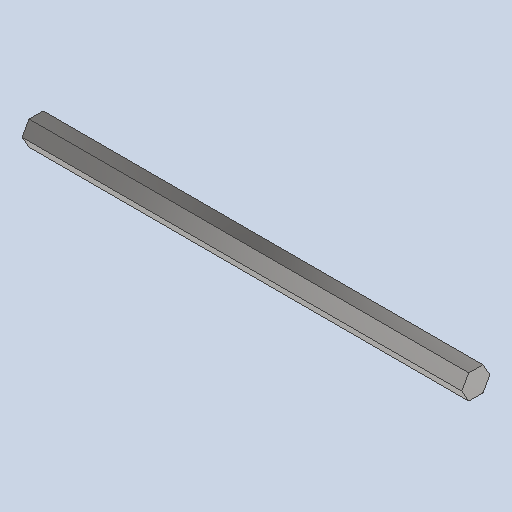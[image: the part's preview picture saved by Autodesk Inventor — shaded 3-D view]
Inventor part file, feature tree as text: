
AUTODESK INVENTOR PART (.ipt)
format: ipt  version: 2023 (Build 270158000, 158)  size: 96,256 bytes
history: native  units: in
note: dims shown in document units (in); Inventor stores cm internally (conversion verified against a paired STEP export)
features: extrude x1, sketch x1
ambient origin geometry x8: Origin, YZ Plane, XZ Plane, XY Plane, X Axis, Y Axis, Z Axis, Center Point
bodies: Solid1 (feature_tree)
feature tree (2):
  extrude  "Extrusion1"  Depth=9.0in TaperAngle=0.0deg
  sketch  "Sketch1"  dims[d0=0.5in d1=9.0in d2=0.0in]
